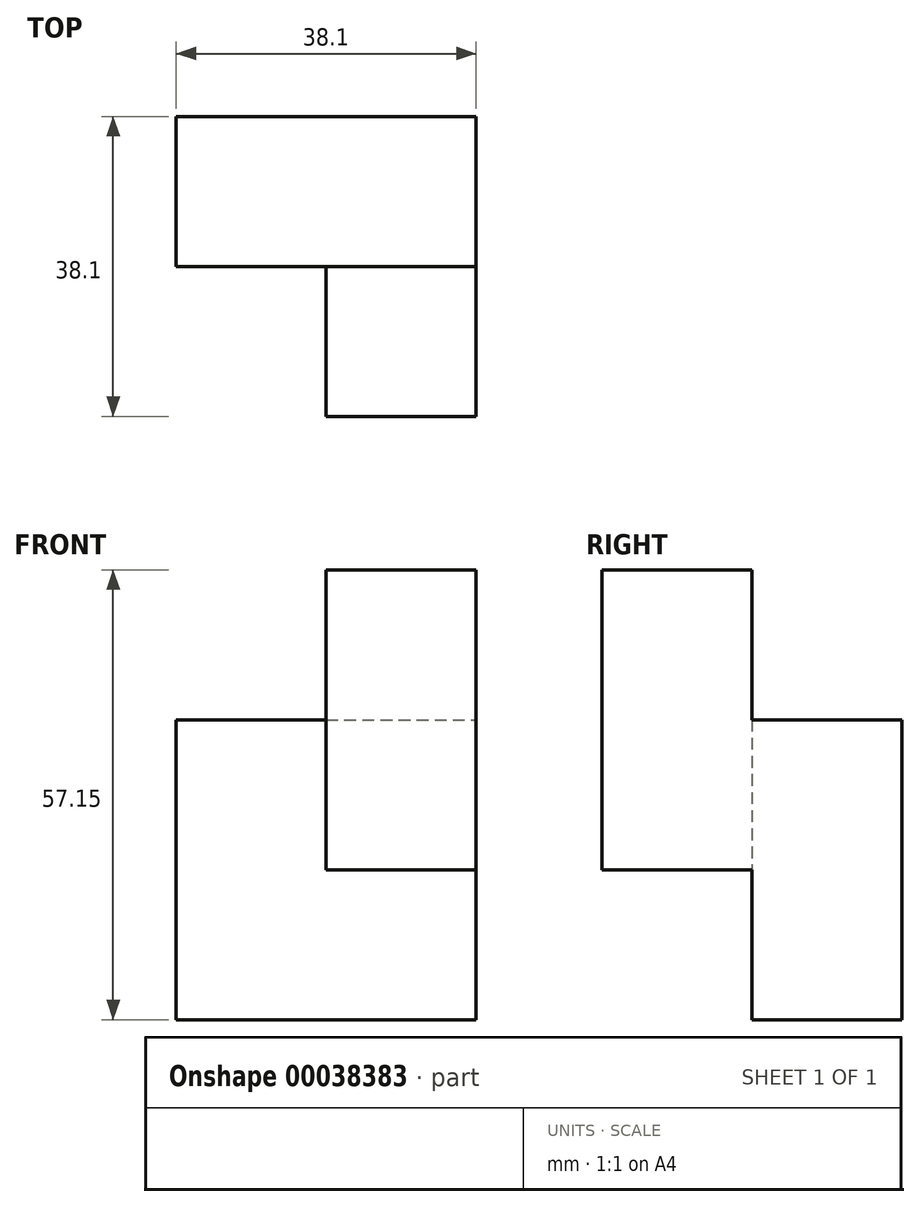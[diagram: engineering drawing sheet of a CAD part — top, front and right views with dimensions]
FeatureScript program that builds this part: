
annotation { "Feature Type Name" : "Feature", "Feature Type Description" : "" }
export const myFeature = defineFeature(function(context is Context, id is Id, definition is map)
    precondition{}
    {
        {
            var Q0;
            Q0=qCreatedBy(makeId("Top.planeOp"),FACE);
            var sketch = newSketch(context, id + "F0", { "sketchPlane" : qUnion([Q0])});
            skLineSegment(sketch, "E0.bottom", {"start": v(0, 0) * mm, "end": v(19.05, 0) * mm});
            skLineSegment(sketch, "E0.top", {"start": v(0, 19.05) * mm, "end": v(19.05, 19.05) * mm});
            skLineSegment(sketch, "E0.left", {"start": v(0, 0) * mm, "end": v(0, 19.05) * mm});
            skLineSegment(sketch, "E0.right", {"start": v(19.05, 0) * mm, "end": v(19.05, 19.05) * mm});
            skSolve(sketch);
        }
        {
            var Q0;
            Q0=makeQuery(id+"F0.imprint","IMPRINT",FACE,{"disambiguationData":[TD([[makeQuery(id+"F0.imprint","IMPRINT",EDGE,{"derivedFrom":sQuery(id+"F0.wireOp",EDGE,"E0.bottom")}),1.0]])]});
            extrude(context, id + "F1", {"entities" : qUnion([Q0]), "depth" : 19.05 * mm});
        }
        {
            var Q0;
            Q0=makeQuery(id+"F1.opExtrude","CAP_FACE",FACE,{"disambiguationData":[OSD([sQuery(id+"F0.wireOp",EDGE,"E0.bottom"),sQuery(id+"F0.wireOp",EDGE,"E0.top"),sQuery(id+"F0.wireOp",EDGE,"E0.left"),sQuery(id+"F0.wireOp",EDGE,"E0.right")])],"isStart":false});
            extrude(context, id + "F2", {"entities" : qUnion([Q0]), "operationType" : NewBodyOperationType.ADD, "depth" : 19.05 * mm});
        }
        {
            var Q0;
            {var subQ0=sQuery(id+"F0.wireOp",EDGE,"E0.bottom");Q0=makeQuery(id+"F2.boolean.opBoolean","MERGE",FACE,{"derivedFrom":[makeQuery(id+"F1.opExtrude","SWEPT_FACE",FACE,{"disambiguationData":[OSD([subQ0])]}),makeQuery(id+"F2.opExtrude","SWEPT_FACE",FACE,{"disambiguationData":[OSD([subQ0])]})]});}
            var sketch = newSketch(context, id + "F3", { "sketchPlane" : qUnion([Q0])});
            skLineSegment(sketch, "E1.bottom", {"start": v(0, 38.1) * mm, "end": v(19.05, 38.1) * mm});
            skLineSegment(sketch, "E1.top", {"start": v(0, 19.05) * mm, "end": v(19.05, 19.05) * mm});
            skLineSegment(sketch, "E1.left", {"start": v(0, 38.1) * mm, "end": v(0, 19.05) * mm});
            skLineSegment(sketch, "E1.right", {"start": v(19.05, 38.1) * mm, "end": v(19.05, 19.05) * mm});
            skSolve(sketch);
        }
        {
            var Q0;
            {var subQ0=sQuery(id+"F0.wireOp",EDGE,"E0.left");Q0=makeQuery(id+"F2.boolean.opBoolean","MERGE",FACE,{"derivedFrom":[makeQuery(id+"F1.opExtrude","SWEPT_FACE",FACE,{"disambiguationData":[OSD([subQ0])]}),makeQuery(id+"F2.opExtrude","SWEPT_FACE",FACE,{"disambiguationData":[OSD([subQ0])]})]});}
            var sketch = newSketch(context, id + "F4", { "sketchPlane" : qUnion([Q0])});
            skLineSegment(sketch, "E2.bottom", {"start": v(-19.05, 0) * mm, "end": v(0, 0) * mm});
            skLineSegment(sketch, "E2.top", {"start": v(-19.05, 19.05) * mm, "end": v(0, 19.05) * mm});
            skLineSegment(sketch, "E2.left", {"start": v(-19.05, 0) * mm, "end": v(-19.05, 19.05) * mm});
            skLineSegment(sketch, "E2.right", {"start": v(0, 0) * mm, "end": v(0, 19.05) * mm});
            skLineSegment(sketch, "E3.bottom", {"start": v(0, 38.1) * mm, "end": v(-19.05, 38.1) * mm});
            skLineSegment(sketch, "E3.top", {"start": v(0, 19.05) * mm, "end": v(-19.05, 19.05) * mm});
            skLineSegment(sketch, "E3.left", {"start": v(0, 38.1) * mm, "end": v(0, 19.05) * mm});
            skLineSegment(sketch, "E3.right", {"start": v(-19.05, 38.1) * mm, "end": v(-19.05, 19.05) * mm});
            skSolve(sketch);
        }
        {
            var Q0;
            Q0=makeQuery(id+"F3.imprint","IMPRINT",FACE,{"disambiguationData":[TD([[makeQuery(id+"F3.imprint","IMPRINT",EDGE,{"derivedFrom":sQuery(id+"F3.wireOp",EDGE,"E1.bottom")}),-1.0]])]});
            extrude(context, id + "F5", {"entities" : qUnion([Q0]), "operationType" : NewBodyOperationType.ADD, "depth" : 19.05 * mm});
        }
        {
            var Q0;
            Q0=makeQuery(id+"F4.imprint","IMPRINT",FACE,{"disambiguationData":[TD([[makeQuery(id+"F4.imprint","IMPRINT",EDGE,{"derivedFrom":sQuery(id+"F4.wireOp",EDGE,"E3.bottom")}),1.0]])]});
            extrude(context, id + "F6", {"entities" : qUnion([Q0]), "operationType" : NewBodyOperationType.ADD, "depth" : 19.05 * mm});
        }
        {
            var Q0;
            {var subQ0=sQuery(id+"F0.wireOp",EDGE,"E0.left");var subQ1=makeQuery(id+"F1.opExtrude","SWEPT_FACE",FACE,{"disambiguationData":[OSD([subQ0])]});var subQ2=makeQuery(id+"F2.opExtrude","SWEPT_FACE",FACE,{"disambiguationData":[OSD([subQ0])]});var subQ3=makeQuery(id+"F5.opExtrude","SWEPT_FACE",FACE,{"disambiguationData":[OSD([sQuery(id+"F3.wireOp",EDGE,"E1.left")])]});var subQ4=sQuery(id+"F0.wireOp",EDGE,"E0.top");Q0=makeQuery(id+"F6.boolean.opBoolean","SPLIT",FACE,{"disambiguationData":[TD([makeQuery(id+"F1.opExtrude","SWEPT_FACE",FACE,{"disambiguationData":[OSD([subQ4])]})])],"derivedFrom":makeQuery(id+"F5.boolean.opBoolean","MERGE",FACE,{"derivedFrom":[makeQuery(id+"F2.boolean.opBoolean","MERGE",FACE,{"derivedFrom":[subQ1,subQ2]}),subQ3]})});}
            extrude(context, id + "F7", {"entities" : qUnion([Q0]), "operationType" : NewBodyOperationType.ADD, "depth" : 19.05 * mm});
        }
        {
            var Q0;
            Q0=makeQuery(id+"F6.boolean.opBoolean","MERGE",FACE,{"derivedFrom":[makeQuery(id+"F5.boolean.opBoolean","MERGE",FACE,{"derivedFrom":[makeQuery(id+"F2.opExtrude","CAP_FACE",FACE,{"disambiguationData":[OSD([sQuery(id+"F0.wireOp",EDGE,"E0.bottom"),sQuery(id+"F0.wireOp",EDGE,"E0.top"),sQuery(id+"F0.wireOp",EDGE,"E0.left"),sQuery(id+"F0.wireOp",EDGE,"E0.right")])],"isStart":false}),makeQuery(id+"F5.opExtrude","SWEPT_FACE",FACE,{"disambiguationData":[OSD([sQuery(id+"F3.wireOp",EDGE,"E1.bottom")])]})]}),makeQuery(id+"F6.opExtrude","SWEPT_FACE",FACE,{"disambiguationData":[OSD([sQuery(id+"F4.wireOp",EDGE,"E3.bottom")])]})]});
            var sketch = newSketch(context, id + "F8", { "sketchPlane" : qUnion([Q0])});
            skLineSegment(sketch, "E4.bottom", {"start": v(-19.05, 19.05) * mm, "end": v(0, 19.05) * mm});
            skLineSegment(sketch, "E4.top", {"start": v(-19.05, 0) * mm, "end": v(0, 0) * mm});
            skLineSegment(sketch, "E4.left", {"start": v(-19.05, 19.05) * mm, "end": v(-19.05, 0) * mm});
            skLineSegment(sketch, "E4.right", {"start": v(0, 19.05) * mm, "end": v(0, 0) * mm});
            skLineSegment(sketch, "E5.bottom", {"start": v(0, 0) * mm, "end": v(19.05, 0) * mm});
            skLineSegment(sketch, "E5.top", {"start": v(0, 19.05) * mm, "end": v(19.05, 19.05) * mm});
            skLineSegment(sketch, "E5.left", {"start": v(0, 0) * mm, "end": v(0, 19.05) * mm});
            skLineSegment(sketch, "E5.right", {"start": v(19.05, 0) * mm, "end": v(19.05, 19.05) * mm});
            skLineSegment(sketch, "E6.top", {"start": v(0, -19.05) * mm, "end": v(19.05, -19.05) * mm});
            skLineSegment(sketch, "E6.left", {"start": v(0, 0) * mm, "end": v(0, -19.05) * mm});
            skLineSegment(sketch, "E6.right", {"start": v(19.05, 0) * mm, "end": v(19.05, -19.05) * mm});
            skSolve(sketch);
        }
        {
            var Q0;
            Q0=makeQuery(id+"F8.imprint","IMPRINT",FACE,{"disambiguationData":[TD([[makeQuery(id+"F8.imprint","IMPRINT",EDGE,{"derivedFrom":sQuery(id+"F8.wireOp",EDGE,"E5.bottom")}),-1.0]])]});
            extrude(context, id + "F9", {"entities" : qUnion([Q0]), "operationType" : NewBodyOperationType.ADD, "depth" : 19.05 * mm});
        }
    });
